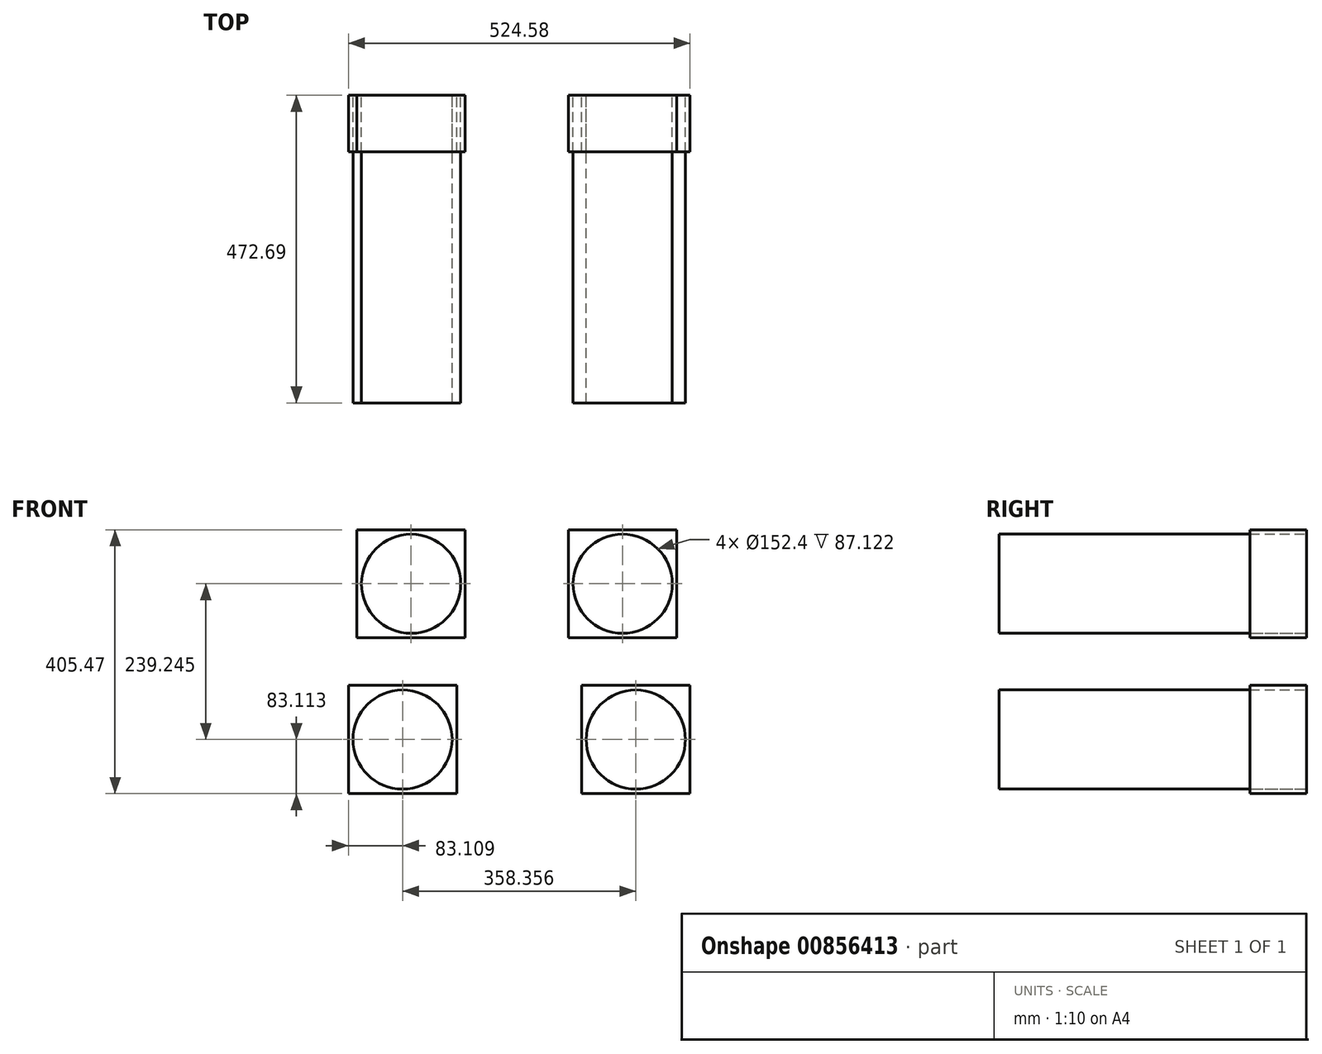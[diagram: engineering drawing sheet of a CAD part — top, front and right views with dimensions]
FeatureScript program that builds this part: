
annotation { "Feature Type Name" : "Feature", "Feature Type Description" : "" }
export const myFeature = defineFeature(function(context is Context, id is Id, definition is map)
    precondition{}
    {
        {
            var Q0;
            Q0=qCreatedBy(makeId("Front.planeOp"),FACE);
            var sketch = newSketch(context, id + "F0", { "sketchPlane" : qUnion([Q0])});
            skCircle(sketch, "E0", {"center": v(-152.97, 108.16) * mm, "radius": 76.2 * mm});
            skCircle(sketch, "E1", {"center": v(172.05, 108.16) * mm, "radius": 76.2 * mm});
            skCircle(sketch, "E2", {"center": v(192.27, -131.09) * mm, "radius": 76.2 * mm});
            skCircle(sketch, "E3", {"center": v(-166.08, -131.09) * mm, "radius": 76.2 * mm});
            skCircle(sketch, "E4.cCircle", {"center": v(-152.97, 108.16) * mm, "radius": 83.11 * mm, "construction": true});
            skLineSegment(sketch, "E4.0", {"start": v(-69.86, 25.05) * mm, "end": v(-236.09, 25.05) * mm});
            skLineSegment(sketch, "E4.1", {"start": v(-236.09, 25.05) * mm, "end": v(-236.09, 191.27) * mm});
            skLineSegment(sketch, "E4.2", {"start": v(-236.09, 191.27) * mm, "end": v(-69.86, 191.27) * mm});
            skLineSegment(sketch, "E4.3", {"start": v(-69.86, 191.27) * mm, "end": v(-69.86, 25.05) * mm});
            skPoint(sketch, "E4.0.midPoint", {"position": v(-152.97, 25.05) * mm});
            skCircle(sketch, "E5.cCircle", {"center": v(-166.08, -131.09) * mm, "radius": 83.11 * mm, "construction": true});
            skLineSegment(sketch, "E5.0", {"start": v(-249.2, -47.97) * mm, "end": v(-82.97, -47.97) * mm});
            skLineSegment(sketch, "E5.1", {"start": v(-82.97, -47.97) * mm, "end": v(-82.97, -214.2) * mm});
            skLineSegment(sketch, "E5.2", {"start": v(-82.97, -214.2) * mm, "end": v(-249.2, -214.2) * mm});
            skLineSegment(sketch, "E5.3", {"start": v(-249.2, -214.2) * mm, "end": v(-249.2, -47.97) * mm});
            skPoint(sketch, "E5.0.midPoint", {"position": v(-166.08, -47.97) * mm});
            skCircle(sketch, "E6.cCircle", {"center": v(192.27, -131.09) * mm, "radius": 83.11 * mm, "construction": true});
            skLineSegment(sketch, "E6.0", {"start": v(109.16, -47.97) * mm, "end": v(275.39, -47.97) * mm});
            skLineSegment(sketch, "E6.1", {"start": v(275.39, -47.97) * mm, "end": v(275.39, -214.2) * mm});
            skLineSegment(sketch, "E6.2", {"start": v(275.39, -214.2) * mm, "end": v(109.16, -214.2) * mm});
            skLineSegment(sketch, "E6.3", {"start": v(109.16, -214.2) * mm, "end": v(109.16, -47.97) * mm});
            skPoint(sketch, "E6.0.midPoint", {"position": v(192.27, -47.97) * mm});
            skCircle(sketch, "E7.cCircle", {"center": v(172.05, 108.16) * mm, "radius": 83.11 * mm, "construction": true});
            skLineSegment(sketch, "E7.0", {"start": v(255.17, 25.05) * mm, "end": v(88.94, 25.05) * mm});
            skLineSegment(sketch, "E7.1", {"start": v(88.94, 25.05) * mm, "end": v(88.94, 191.27) * mm});
            skLineSegment(sketch, "E7.2", {"start": v(88.94, 191.27) * mm, "end": v(255.17, 191.27) * mm});
            skLineSegment(sketch, "E7.3", {"start": v(255.17, 191.27) * mm, "end": v(255.17, 25.05) * mm});
            skPoint(sketch, "E7.0.midPoint", {"position": v(172.05, 25.05) * mm});
            skSolve(sketch);
        }
        {
            var Q0;
            Q0=makeQuery(id+"F0.imprint","IMPRINT",FACE,{"disambiguationData":[TD([[makeQuery(id+"F0.imprint","IMPRINT",EDGE,{"derivedFrom":sQuery(id+"F0.wireOp",EDGE,"E0")}),-1.0]])]});
            var Q1;
            Q1=makeQuery(id+"F0.imprint","IMPRINT",FACE,{"disambiguationData":[TD([[makeQuery(id+"F0.imprint","IMPRINT",EDGE,{"derivedFrom":sQuery(id+"F0.wireOp",EDGE,"E3")}),-1.0]])]});
            var Q2;
            Q2=makeQuery(id+"F0.imprint","IMPRINT",FACE,{"disambiguationData":[TD([[makeQuery(id+"F0.imprint","IMPRINT",EDGE,{"derivedFrom":sQuery(id+"F0.wireOp",EDGE,"E2")}),-1.0]])]});
            var Q3;
            Q3=makeQuery(id+"F0.imprint","IMPRINT",FACE,{"disambiguationData":[TD([[makeQuery(id+"F0.imprint","IMPRINT",EDGE,{"derivedFrom":sQuery(id+"F0.wireOp",EDGE,"E1")}),-1.0]])]});
            extrude(context, id + "F1", {"entities" : qUnion([Q0, Q1, Q2, Q3]), "depth" : 87.12 * mm, "offsetDistance" : 25.4 * mm});
        }
        {
            var Q0;
            Q0=makeQuery(id+"F0.imprint","IMPRINT",FACE,{"disambiguationData":[TD([[makeQuery(id+"F0.imprint","IMPRINT",EDGE,{"derivedFrom":sQuery(id+"F0.wireOp",EDGE,"E3")}),1.0]])]});
            var Q1;
            Q1=makeQuery(id+"F0.imprint","IMPRINT",FACE,{"disambiguationData":[TD([[makeQuery(id+"F0.imprint","IMPRINT",EDGE,{"derivedFrom":sQuery(id+"F0.wireOp",EDGE,"E0")}),1.0]])]});
            var Q2;
            Q2=makeQuery(id+"F0.imprint","IMPRINT",FACE,{"disambiguationData":[TD([[makeQuery(id+"F0.imprint","IMPRINT",EDGE,{"derivedFrom":sQuery(id+"F0.wireOp",EDGE,"E1")}),1.0]])]});
            var Q3;
            Q3=makeQuery(id+"F0.imprint","IMPRINT",FACE,{"disambiguationData":[TD([[makeQuery(id+"F0.imprint","IMPRINT",EDGE,{"derivedFrom":sQuery(id+"F0.wireOp",EDGE,"E2")}),1.0]])]});
            extrude(context, id + "F2", {"entities" : qUnion([Q0, Q1, Q2, Q3]), "depth" : 472.7 * mm, "offsetDistance" : 25.4 * mm});
        }
    });
